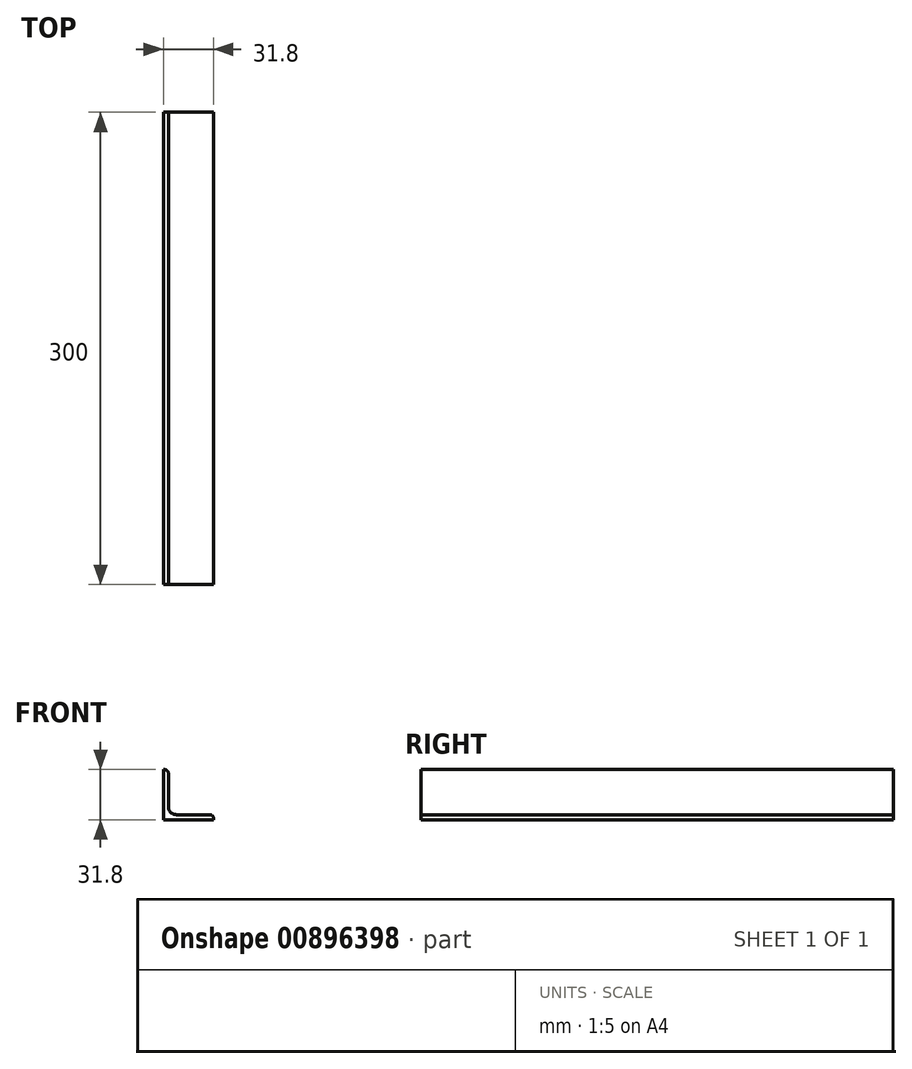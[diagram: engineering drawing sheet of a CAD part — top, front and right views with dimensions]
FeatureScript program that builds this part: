
annotation { "Feature Type Name" : "Feature", "Feature Type Description" : "" }
export const myFeature = defineFeature(function(context is Context, id is Id, definition is map)
    precondition{}
    {
        {
            var Q0;
            Q0=qCreatedBy(makeId("Front.planeOp"),FACE);
            var sketch = newSketch(context, id + "F0", { "sketchPlane" : qUnion([Q0])});
            skLineSegment(sketch, "E0", {"start": v(-10.15, 31.8) * mm, "end": v(-10.15, 0) * mm});
            skLineSegment(sketch, "E1", {"start": v(-10.15, 0) * mm, "end": v(21.65, 0) * mm});
            skLineSegment(sketch, "E2", {"start": v(21.65, 0) * mm, "end": v(21.65, 0.67) * mm});
            skLineSegment(sketch, "E3", {"start": v(19.15, 3.17) * mm, "end": v(-1.98, 3.17) * mm});
            skLineSegment(sketch, "E4", {"start": v(-6.98, 8.17) * mm, "end": v(-6.98, 29.3) * mm});
            skLineSegment(sketch, "E5", {"start": v(-9.48, 31.8) * mm, "end": v(-10.15, 31.8) * mm});
            skPoint(sketch, "E6.visualSharp", {"position": v(-6.98, 31.8) * mm});
            skArc(sketch, "E6.filletArc", {"start": v(-6.98, 29.3) * mm, "mid": v(-7.71, 31.07) * mm, "end": v(-9.48, 31.8) * mm});
            skPoint(sketch, "E7.visualSharp", {"position": v(21.65, 3.17) * mm});
            skArc(sketch, "E7.filletArc", {"start": v(21.65, 0.67) * mm, "mid": v(20.92, 2.44) * mm, "end": v(19.15, 3.17) * mm});
            skPoint(sketch, "E8.visualSharp", {"position": v(-6.98, 3.17) * mm});
            skArc(sketch, "E8.filletArc", {"start": v(-6.98, 8.17) * mm, "mid": v(-5.52, 4.63) * mm, "end": v(-1.98, 3.17) * mm});
            skSolve(sketch);
        }
        {
            var Q0;
            Q0=makeQuery(id+"F0.imprint","IMPRINT",FACE,{"disambiguationData":[TD([[makeQuery(id+"F0.imprint","IMPRINT",EDGE,{"derivedFrom":sQuery(id+"F0.wireOp",EDGE,"E0")}),1.0]])]});
            extrude(context, id + "F1", {"entities" : qUnion([Q0]), "depth" : 300 * mm, "offsetDistance" : 25 * mm});
        }
    });
